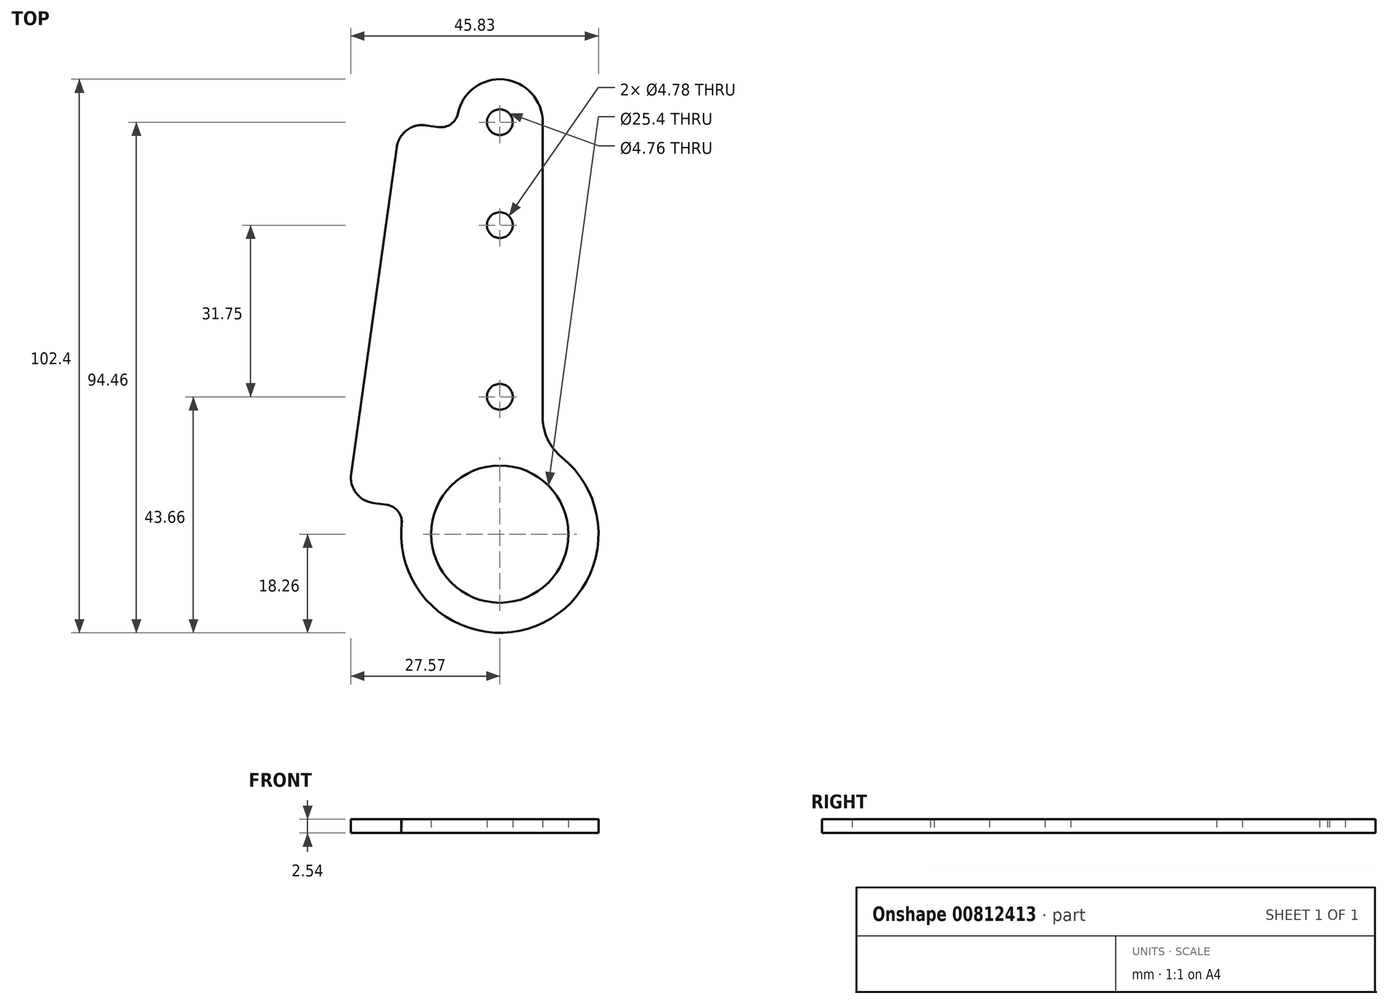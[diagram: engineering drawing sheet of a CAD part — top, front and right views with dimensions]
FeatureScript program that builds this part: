
annotation { "Feature Type Name" : "Feature", "Feature Type Description" : "" }
export const myFeature = defineFeature(function(context is Context, id is Id, definition is map)
    precondition{}
    {
        {
            var Q0;
            Q0=qCreatedBy(makeId("Top.planeOp"),FACE);
            var sketch = newSketch(context, id + "F0", { "sketchPlane" : qUnion([Q0])});
            skCircle(sketch, "E0", {"center": v(0, 0) * mm, "radius": 12.7 * mm});
            skArc(sketch, "E1", {"start": v(-18.08, 2.53) * mm, "mid": v(6.7, -16.98) * mm, "end": v(11.47, 14.2) * mm});
            skCircle(sketch, "E2", {"center": v(0, 76.2) * mm, "radius": 2.38 * mm});
            skArc(sketch, "E3", {"start": v(7.94, 76.2) * mm, "mid": v(0.8, 84.1) * mm, "end": v(-7.78, 77.8) * mm});
            skCircle(sketch, "E4", {"center": v(0, 57.15) * mm, "radius": 2.39 * mm});
            skCircle(sketch, "E5", {"center": v(0, 25.4) * mm, "radius": 2.39 * mm});
            skLineSegment(sketch, "E6.0", {"start": v(7.94, 76.2) * mm, "end": v(7.93, 21.62) * mm});
            skArc(sketch, "E7", {"start": v(7.93, 21.62) * mm, "mid": v(8.86, 17.5) * mm, "end": v(11.47, 14.2) * mm});
            skLineSegment(sketch, "E8", {"start": v(7.94, 76.2) * mm, "end": v(-7.78, 76.2) * mm});
            skLineSegment(sketch, "E9.0", {"start": v(-19.07, 71.57) * mm, "end": v(-27.52, 11.15) * mm});
            skLineSegment(sketch, "E10", {"start": v(-23.47, 5.77) * mm, "end": v(-20.88, 5.41) * mm});
            skLineSegment(sketch, "E11", {"start": v(-13.7, 75.62) * mm, "end": v(-11.33, 75.3) * mm});
            skArc(sketch, "E12", {"start": v(-13.7, 75.62) * mm, "mid": v(-17.23, 74.7) * mm, "end": v(-19.07, 71.57) * mm});
            skPoint(sketch, "E13.orphan", {"position": v(-18.42, 76.28) * mm});
            skArc(sketch, "E14", {"start": v(-27.52, 11.15) * mm, "mid": v(-26.6, 7.62) * mm, "end": v(-23.47, 5.77) * mm});
            skPoint(sketch, "E15.orphan", {"position": v(-28.18, 6.43) * mm});
            skLineSegment(sketch, "E16.trimOffspring", {"start": v(-18.08, 2.53) * mm, "end": v(-18.18, 1.83) * mm});
            skArc(sketch, "E17", {"start": v(-18.18, 1.83) * mm, "mid": v(-18.79, 4.18) * mm, "end": v(-20.88, 5.41) * mm});
            skPoint(sketch, "E18.orphan", {"position": v(-18.43, 0) * mm});
            skArc(sketch, "E19", {"start": v(-11.33, 75.3) * mm, "mid": v(-9.05, 75.84) * mm, "end": v(-7.78, 77.8) * mm});
            skSolve(sketch);
        }
        {
            var Q0;
            Q0=makeQuery(id+"F0.imprint","IMPRINT",FACE,{"disambiguationData":[TD([[makeQuery(id+"F0.imprint","IMPRINT",EDGE,{"derivedFrom":sQuery(id+"F0.wireOp",EDGE,"E0")}),-1.0]])]});
            extrude(context, id + "F1", {"entities" : qUnion([Q0]), "depth" : 2.54 * mm, "offsetDistance" : 25.4 * mm});
        }
    });
